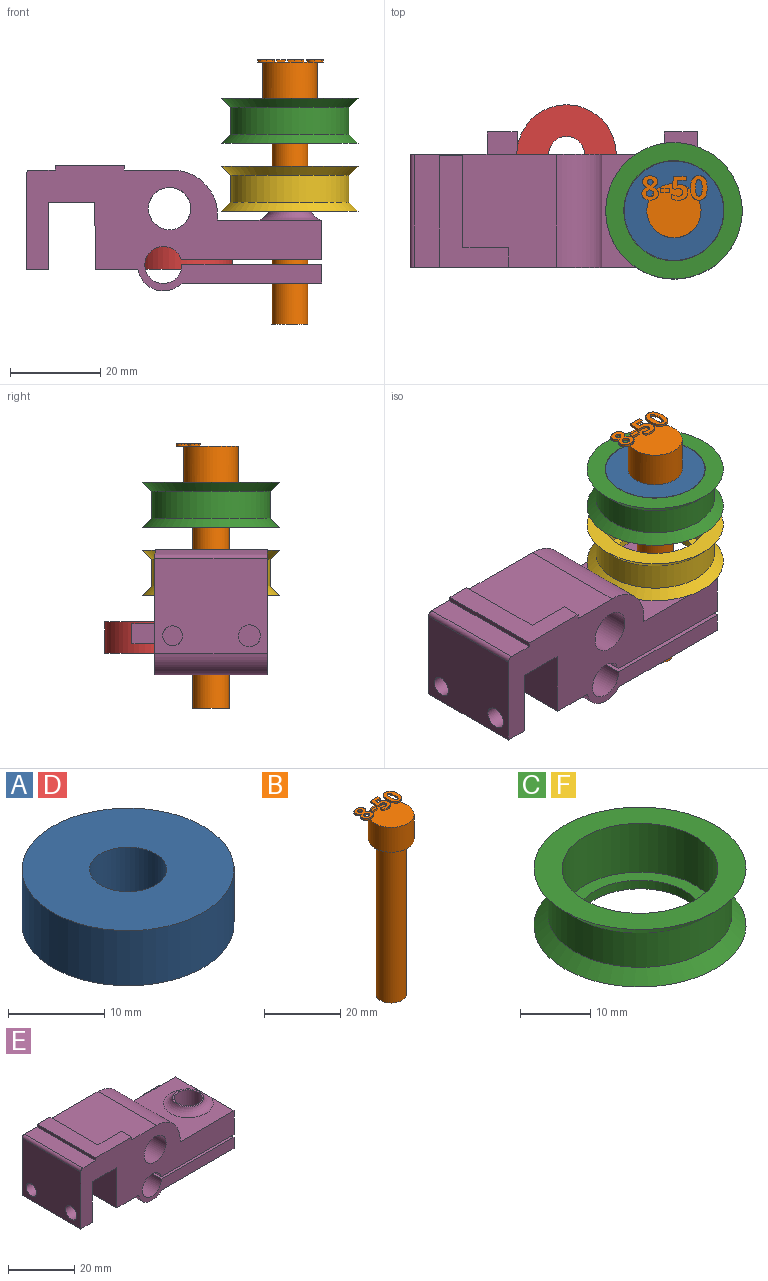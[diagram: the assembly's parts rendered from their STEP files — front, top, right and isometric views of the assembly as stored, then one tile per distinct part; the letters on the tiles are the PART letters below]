
ASSEMBLY  parts=6 mates=4
PART A: 4 faces, bbox 22x22x7 mm
  f0: cylinder r=4mm len=8mm, axis (0,0,-1), area 175.9mm2, adj f2,f3
  f1: cylinder r=11mm len=22mm, axis (0,0,-1), area 483.8mm2, adj f2,f3
  f2: plane 22x22mm, normal (0,0,1), area 329.9mm2, adj f0,f1
  f3: plane 22x22mm, normal (0,0,-1), area 329.9mm2, adj f0,f1
PART B: 86 faces, bbox 14.5x13.7x58.5 mm
  f0: plane 12x12mm, normal (0,0,1), area 99.4mm2, adj f5,f22,f23,f24,f25,f26,f40,f41
  f1: plane 1x0.26mm, normal (0,0,1), area 0.1mm2, adj f5,f46,f47,f48,f49
  f2: plane 0.85x0.68mm, normal (0,0,1), area 0.2mm2, adj f5,f29,f30,f31
  f3: cylinder r=4mm len=50mm, axis (0,0,-1), area 1256.6mm2, adj f4,f6
  f4: plane 8x8mm, normal (0,0,-1), area 50.3mm2, adj f3
  f5: cylinder r=6mm len=12mm, axis (0,0,-1), area 301.6mm2, adj f0,f1,f2,f6,f39,f45,f67,f85
  f6: plane 12x12mm, normal (0,0,-1), area 62.8mm2, adj f3,f5
  f7: extruded ~0.5x0.46mm, area 0.2mm2, adj f8,f37,f38,f39
  f8: extruded ~0.5x0.46mm, area 0.2mm2, adj f7,f9,f38,f39
  f9: extruded ~0.5x0.39mm, area 0.2mm2, adj f8,f10,f38,f39
  f10: extruded ~0.5x0.4mm, area 0.2mm2, adj f9,f11,f38,f39
  f11: extruded ~0.5x0.49mm, area 0.3mm2, adj f10,f12,f38,f39
  f12: extruded ~0.5x0.5mm, area 0.3mm2, adj f11,f13,f38,f39
  f13: extruded ~0.5x0.39mm, area 0.2mm2, adj f12,f37,f38,f39
  f14: extruded ~1.22x0.5mm, area 0.6mm2, adj f15,f35,f38,f39
  f15: extruded ~1.22x0.5mm, area 0.6mm2, adj f14,f16,f38,f39
  f16: extruded ~0.91x0.5mm, area 0.5mm2, adj f15,f17,f38,f39
  f17: extruded ~0.71x0.5mm, area 0.4mm2, adj f16,f18,f38,f39
  f18: extruded ~0.65x0.61mm, area 0.4mm2, adj f17,f19,f38,f39
  f19: extruded ~0.77x0.62mm, area 0.5mm2, adj f18,f20,f38,f39
  f20: extruded ~0.8x0.5mm, area 0.4mm2, adj f19,f21,f38,f39
  f21: extruded ~1.04x0.5mm, area 0.6mm2, adj f20,f22,f38,f39
  f22: extruded ~1.36x0.5mm, area 0.7mm2, adj f0,f21,f23,f38,f39
  f23: extruded ~1.33x0.5mm, area 0.7mm2, adj f0,f22,f24,f38
  f24: extruded ~1.04x0.51mm, area 0.6mm2, adj f0,f23,f25,f38
  f25: extruded ~0.75x0.5mm, area 0.4mm2, adj f0,f24,f26,f38
  f26: extruded ~0.85x0.66mm, area 0.5mm2, adj f0,f25,f27,f38,f39
  f27: extruded ~0.72x0.56mm, area 0.5mm2, adj f26,f28,f38,f39
  f28: extruded ~0.72x0.5mm, area 0.4mm2, adj f27,f35,f38,f39
  f29: extruded ~0.5x0.45mm, area 0.3mm2, adj f2,f30,f36,f38,f39
  f30: extruded ~0.5x0.47mm, area 0.3mm2, adj f2,f29,f31,f38
  f31: extruded ~0.62x0.5mm, area 0.3mm2, adj f2,f30,f32,f38,f39
  f32: extruded ~0.59x0.5mm, area 0.3mm2, adj f31,f33,f38,f39
  f33: extruded ~0.5x0.48mm, area 0.3mm2, adj f32,f34,f38,f39
  f34: extruded ~0.89x0.77mm, area 0.6mm2, adj f33,f36,f38,f39
  f35: extruded ~0.93x0.5mm, area 0.5mm2, adj f14,f28,f38,f39
  f36: extruded ~0.66x0.5mm, area 0.4mm2, adj f29,f34,f38,f39
  f37: extruded ~0.5x0.39mm, area 0.2mm2, adj f7,f13,f38,f39
  f38: plane 5.4x3.69mm, normal (0,0,1), area 12.7mm2, adj f7,f8,f9,f10,f11,f12,f13,f14
  f39: plane 5.4x3.53mm, normal (0,0,-1), area 10.2mm2, adj f5,f7,f8,f9,f10,f11,f12,f13
  f40: plane 0.9x0.5mm, normal (-1,0,0), area 0.4mm2, adj f0,f41,f43,f44
  f41: plane 1.93x0.5mm, normal (0,-1,0), area 1mm2, adj f0,f40,f42,f44
  f42: plane 0.9x0.5mm, normal (1,0,0), area 0.4mm2, adj f0,f41,f43,f44
  f43: plane 1.93x0.5mm, normal (0,1,0), area 1mm2, adj f0,f40,f42,f44
  f44: plane 1.93x0.9mm, normal (0,0,1), area 1.7mm2, adj f40,f41,f42,f43
  f45: plane 0.76x0.31mm, normal (0,0,-1), area 0mm2, adj f5,f46
  f46: extruded ~1.21x0.5mm, area 0.7mm2, adj f0,f1,f45,f47,f65,f66
  f47: extruded ~0.54x0.5mm, area 0.3mm2, adj f1,f46,f48,f66
  f48: plane 0.5x0.13mm, normal (-0.2,0.98,0), area 0.1mm2, adj f1,f47,f49,f66
  f49: plane 1.03x0.5mm, normal (1,-0.09,0), area 0.5mm2, adj f1,f48,f50,f66,f67
  f50: plane 1.88x0.5mm, normal (0,-1,0), area 0.9mm2, adj f49,f51,f66,f67
  f51: plane 0.94x0.5mm, normal (1,0,0), area 0.5mm2, adj f50,f52,f66,f67
  f52: plane 2.85x0.5mm, normal (0,1,0), area 1.4mm2, adj f51,f53,f66,f67
  f53: plane 2.68x0.5mm, normal (-1,0.07,0), area 1.3mm2, adj f0,f52,f54,f66,f67
  f54: plane 0.5x0.44mm, normal (-0.47,-0.88,0), area 0.3mm2, adj f0,f53,f55,f66
  f55: extruded ~0.5x0.37mm, area 0.2mm2, adj f0,f54,f56,f66
  f56: extruded ~0.5x0.42mm, area 0.2mm2, adj f0,f55,f57,f66
  f57: extruded ~1.05x0.8mm, area 0.8mm2, adj f0,f56,f58,f66
  f58: extruded ~1.02x0.83mm, area 0.8mm2, adj f0,f57,f59,f66
  f59: extruded ~0.72x0.5mm, area 0.4mm2, adj f0,f58,f60,f66
  f60: extruded ~0.66x0.5mm, area 0.4mm2, adj f0,f59,f61,f66
  f61: plane 0.96x0.5mm, normal (-1,0,0), area 0.5mm2, adj f0,f60,f62,f66
  f62: extruded ~1.42x0.5mm, area 0.7mm2, adj f0,f61,f63,f66
  f63: extruded ~1.55x0.5mm, area 0.8mm2, adj f0,f62,f64,f66
  f64: extruded ~1.36x0.54mm, area 0.8mm2, adj f0,f63,f65,f66
  f65: extruded ~1.17x0.5mm, area 0.6mm2, adj f0,f46,f64,f66
  f66: plane 5.33x3.51mm, normal (0,0,1), area 10.9mm2, adj f46,f47,f48,f49,f50,f51,f52,f53
  f67: plane 2.97x1.71mm, normal (0,0,-1), area 3.5mm2, adj f5,f49,f50,f51,f52,f53
  f68: extruded ~1.39x0.5mm, area 0.7mm2, adj f69,f83,f84,f85
  f69: extruded ~1.39x0.5mm, area 0.7mm2, adj f68,f70,f84,f85
  f70: extruded ~0.56x0.5mm, area 0.4mm2, adj f69,f71,f84,f85
  f71: extruded ~0.56x0.5mm, area 0.4mm2, adj f70,f72,f84,f85
  f72: extruded ~1.39x0.5mm, area 0.7mm2, adj f71,f73,f84,f85
  f73: extruded ~1.38x0.5mm, area 0.7mm2, adj f72,f74,f84,f85
  f74: extruded ~0.56x0.5mm, area 0.4mm2, adj f73,f83,f84,f85
  f75: extruded ~2.04x0.5mm, area 1.1mm2, adj f76,f82,f84,f85
  f76: extruded ~2.02x0.5mm, area 1.1mm2, adj f75,f77,f84,f85
  f77: extruded ~1.38x0.69mm, area 0.8mm2, adj f76,f78,f84,f85
  f78: extruded ~1.38x0.66mm, area 0.8mm2, adj f77,f79,f84,f85
  f79: extruded ~2.05x0.5mm, area 1.1mm2, adj f78,f80,f84,f85
  f80: extruded ~2.02x0.5mm, area 1mm2, adj f0,f79,f81,f84,f85
  f81: extruded ~1.37x0.68mm, area 0.8mm2, adj f0,f80,f82,f84
  f82: extruded ~1.39x0.66mm, area 0.8mm2, adj f0,f75,f81,f84,f85
  f83: extruded ~0.56x0.5mm, area 0.4mm2, adj f68,f74,f84,f85
  f84: plane 5.41x3.68mm, normal (0,0,1), area 12.1mm2, adj f68,f69,f70,f71,f72,f73,f74,f75
  f85: plane 5.41x3.68mm, normal (0,0,-1), area 10.3mm2, adj f5,f68,f69,f70,f71,f72,f73,f74
PART C: 8 faces, bbox 30.2x30.2x10 mm
  f0: plane 30.2x30.2mm, normal (0,0,1), area 329.2mm2, adj f1,f7
  f1: cylinder r=11.1mm len=22.2mm, axis (0,0,-1), area 592.8mm2, adj f0,f2
  f2: plane 22.2x22.2mm, normal (0,0,1), area 126.9mm2, adj f1,f3
  f3: cylinder r=9.1mm len=18.2mm, axis (0,0,-1), area 85.8mm2, adj f2,f4
  f4: plane 30.2x30.2mm, normal (0,0,-1), area 456.2mm2, adj f3,f5
  f5: cone r=13.1mm half-angle=45deg, axis (0,0,-1), area 250.6mm2, adj f4,f6
  f6: cylinder r=13.1mm len=26.2mm, axis (0,0,-1), area 493.9mm2, adj f5,f7
  f7: cone r=15.1mm half-angle=45deg, axis (0,0,1), area 250.6mm2, adj f0,f6
PART D: same geometry as A
PART E: 42 faces, bbox 68.9x30x27.7 mm
  f0: plane 25x4.12mm, normal (1,0,0), area 103mm2, adj f3,f13,f14,f18
  f1: cylinder r=4.17mm len=8.35mm, axis (0,0,1), area 108.1mm2, adj f3,f18
  f2: plane 25x9.34mm, normal (0,0,-1), area 233.4mm2, adj f12,f13,f14,f16
  f3: plane 30.88x25mm, normal (0,0,-1), area 717.2mm2, adj f0,f1,f13,f14,f16
  f4: plane 25x8.82mm, normal (1,0,0), area 219.6mm2, adj f5,f13,f14,f19,f23
  f5: plane 25x23mm, normal (0,0,1), area 400mm2, adj f4,f6,f13,f14,f23
  f6: plane 25x1.1mm, normal (1,0,0), area 27.5mm2, adj f5,f13,f14,f24
  f7: plane 31.42x25mm, normal (0,0,1), area 611.6mm2, adj f13,f14,f24,f26,f36,f37,f38,f39
  f8: plane 25x21.09mm, normal (-1,0,0), area 493.5mm2, adj f9,f13,f14,f21,f22,f26
  f9: plane 25x5mm, normal (0,0,-1), area 125mm2, adj f8,f10,f13,f14
  f10: plane 25x15mm, normal (1,0,0), area 341.3mm2, adj f9,f11,f13,f14,f21,f22
  f11: plane 25x10.2mm, normal (0,0,-1), area 255mm2, adj f10,f12,f13,f14
  f12: plane 25x14.91mm, normal (-1,0,-0.01), area 372.8mm2, adj f2,f11,f13,f14
  f13: plane 65.42x27.75mm, normal (0,-1,0), area 1002.1mm2, adj f0,f2,f3,f4,f5,f6,f7,f8
  f14: plane 65.42x26.75mm, normal (0,1,0), area 926.8mm2, adj f0,f2,f3,f4,f5,f6,f7,f8
  f15: cylinder r=4.17mm len=10.78mm, axis (0,0,1), area 282.8mm2, adj f19,f20
  f16: cylinder r=5.75mm len=25mm, axis (0,-1,0), area 315.9mm2, adj f2,f3,f13,f14
  f17: cylinder r=4.1mm len=25mm, axis (0,-1,0), area 618.7mm2, adj f13,f14,f18,f19
  f18: plane 30.91x25mm, normal (0,0,1), area 718.1mm2, adj f0,f1,f13,f14,f17
  f19: plane 31.07x30mm, normal (0,0,-1), area 758.4mm2, adj f4,f13,f14,f15,f17,f28,f29,f30
  f20: plane 9.35x9.35mm, normal (0,0,1), area 13.9mm2, adj f15,f23
  f21: cylinder r=2.43mm len=5mm, axis (-1,0,0), area 76.2mm2, adj f8,f10
  f22: cylinder r=2.2mm len=5mm, axis (-1,0,0), area 69.1mm2, adj f8,f10
  f23: torus R=7.5mm, axis (0,0,-1), area 134.6mm2, adj f4,f5,f20
  f24: cylinder r=10mm len=25mm, axis (0,-1,0), area 392.7mm2, adj f6,f7,f13,f14
  f25: cylinder r=4.68mm len=25mm, axis (0,-1,0), area 735.2mm2, adj f13,f14
  f26: cylinder r=1mm len=25mm, axis (0,-1,0), area 39.3mm2, adj f7,f8,f13,f14
  f27: plane 7.3x5mm, normal (0,0,1), area 36.5mm2, adj f14,f28,f29,f30
  f28: plane 5x4.12mm, normal (1,0,0), area 20.6mm2, adj f14,f19,f27,f30
  f29: plane 5x4.12mm, normal (-1,0,0), area 20.6mm2, adj f14,f19,f27,f30
  f30: plane 7.3x4.12mm, normal (0,1,0), area 30.1mm2, adj f19,f27,f28,f29
  f31: plane 6.63x5mm, normal (0,0,1), area 33.2mm2, adj f14,f32,f34,f35
  f32: plane 5x4.5mm, normal (1,0,0), area 22.5mm2, adj f14,f31,f33,f35
  f33: plane 6.63x5mm, normal (0,0,-1), area 33.2mm2, adj f14,f32,f34,f35
  f34: plane 5x4.5mm, normal (-1,0,0), area 22.5mm2, adj f14,f31,f33,f35
  f35: plane 6.63x4.5mm, normal (0,1,0), area 29.9mm2, adj f31,f32,f33,f34
  f36: plane 24.79x1mm, normal (-1,0,0), area 24.8mm2, adj f7,f13,f40,f41
  f37: plane 4.34x1mm, normal (1,0,0), area 4.3mm2, adj f7,f13,f38,f41
  f38: plane 10.05x1mm, normal (0,1,0), area 10.1mm2, adj f7,f37,f39,f41
  f39: plane 20.45x1mm, normal (1,0,0), area 20.4mm2, adj f7,f38,f40,f41
  f40: plane 5.26x1mm, normal (0,1,0), area 5.3mm2, adj f7,f36,f39,f41
  f41: plane 24.79x15.31mm, normal (0,0,1), area 174mm2, adj f13,f36,f37,f38,f39,f40
PART F: same geometry as C
PLACE A t=(23.78,-12.5,30.9)mm
PLACE B t=(23.78,-12.5,-12.1)mm
PLACE C t=(23.78,-12.5,33.1)mm
PLACE D at identity
PLACE E at identity
PLACE F t=(23.78,-12.5,18.1)mm
MATE fastened B.f3 <-> C.f1  axis (0,0,-1) through (23.78,-12.5,37.9)mm
MATE fastened A.f0 <-> C.f1  axis (0,0,1) through (23.78,-12.5,37.9)mm
MATE fastened C.f1 <-> F.f1  axis (0,0,-1) through (23.78,-12.5,27.9)mm
MATE fastened F.f1 <-> E.f1  axis (0,0,-1) through (23.78,-12.5,12.9)mm
